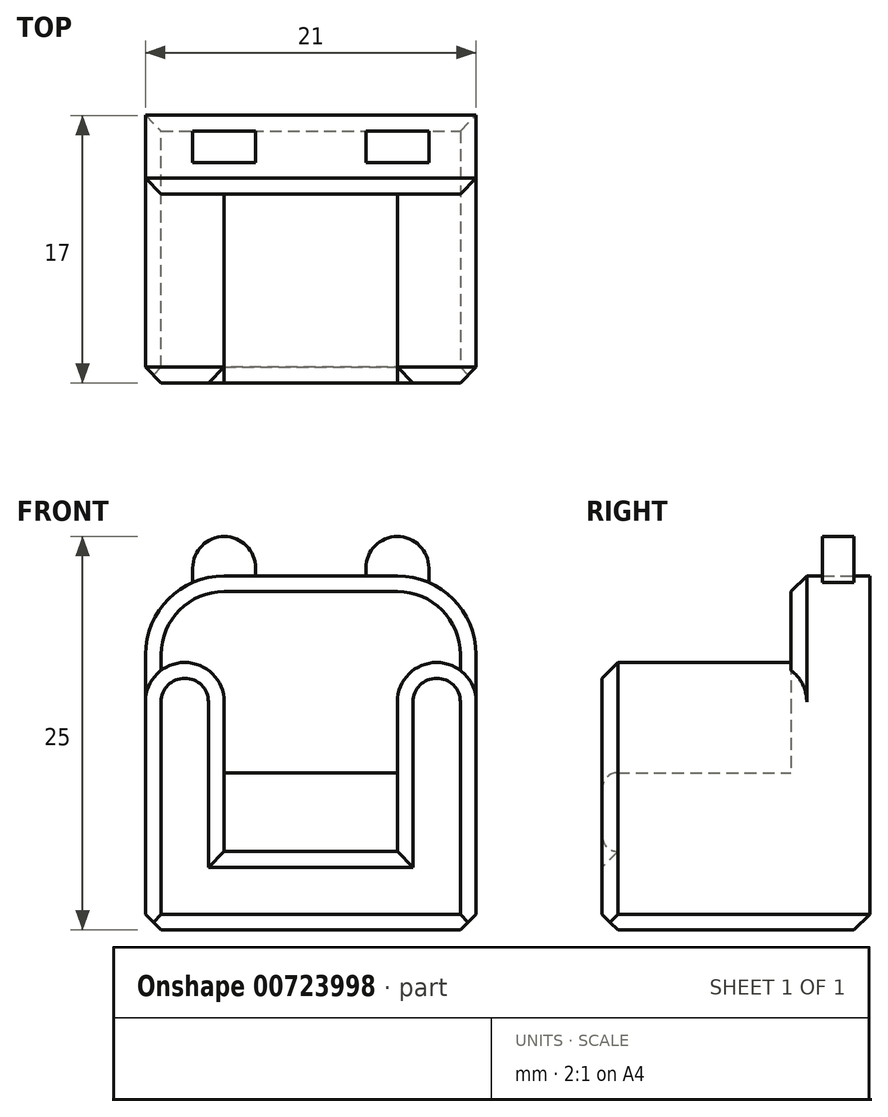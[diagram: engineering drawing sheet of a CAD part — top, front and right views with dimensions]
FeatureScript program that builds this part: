
annotation { "Feature Type Name" : "Feature", "Feature Type Description" : "" }
export const myFeature = defineFeature(function(context is Context, id is Id, definition is map)
    precondition{}
    {
        {
            var Q0;
            Q0=qCreatedBy(makeId("Top.planeOp"),FACE);
            var sketch = newSketch(context, id + "F0", { "sketchPlane" : qUnion([Q0])});
            skLineSegment(sketch, "E0.bottom", {"start": v(-12.68, 6.08) * mm, "end": v(8.32, 6.08) * mm});
            skLineSegment(sketch, "E0.top", {"start": v(-12.68, -10.92) * mm, "end": v(8.32, -10.92) * mm});
            skLineSegment(sketch, "E0.left", {"start": v(-12.68, 6.08) * mm, "end": v(-12.68, -10.92) * mm});
            skLineSegment(sketch, "E0.right", {"start": v(8.32, 6.08) * mm, "end": v(8.32, -10.92) * mm});
            skSolve(sketch);
        }
        {
            var Q0;
            Q0 = qSketchRegion(id + "F0", true);
            extrude(context, id + "F1", {"entities" : qUnion([Q0]), "depth" : 5 * mm, "offsetDistance" : 25 * mm});
        }
        {
            var Q0;
            Q0=makeQuery(id+"F1.opExtrude","CAP_FACE",FACE,{"disambiguationData":[OSD([sQuery(id+"F0.wireOp",EDGE,"E0.bottom"),sQuery(id+"F0.wireOp",EDGE,"E0.top"),sQuery(id+"F0.wireOp",EDGE,"E0.left"),sQuery(id+"F0.wireOp",EDGE,"E0.right")])],"isStart":false});
            var sketch = newSketch(context, id + "F2", { "sketchPlane" : qUnion([Q0])});
            skLineSegment(sketch, "E1.bottom", {"start": v(-12.68, 6.08) * mm, "end": v(8.32, 6.08) * mm});
            skLineSegment(sketch, "E1.top", {"start": v(-12.68, 1.08) * mm, "end": v(8.32, 1.08) * mm});
            skLineSegment(sketch, "E1.left", {"start": v(-12.68, 6.08) * mm, "end": v(-12.68, 1.08) * mm});
            skLineSegment(sketch, "E1.right", {"start": v(8.32, 6.08) * mm, "end": v(8.32, 1.08) * mm});
            skSolve(sketch);
        }
        {
            var Q0;
            Q0 = qSketchRegion(id + "F2", true);
            extrude(context, id + "F3", {"entities" : qUnion([Q0]), "operationType" : NewBodyOperationType.ADD, "depth" : 15 * mm, "offsetDistance" : 25 * mm});
        }
        {
            var Q0;
            Q0=makeQuery(id+"F1.opExtrude","SWEPT_FACE",FACE,{"disambiguationData":[OSD([sQuery(id+"F0.wireOp",EDGE,"E0.top")])]});
            var sketch = newSketch(context, id + "F4", { "sketchPlane" : qUnion([Q0])});
            skLineSegment(sketch, "E2.bottom", {"start": v(-12.68, 0) * mm, "end": v(-7.68, 0) * mm});
            skLineSegment(sketch, "E2.top", {"start": v(-12.68, 17) * mm, "end": v(-7.68, 17) * mm});
            skLineSegment(sketch, "E2.left", {"start": v(-12.68, 0) * mm, "end": v(-12.68, 17) * mm});
            skLineSegment(sketch, "E2.right", {"start": v(-7.68, 0) * mm, "end": v(-7.68, 17) * mm});
            skSolve(sketch);
        }
        {
            var Q0;
            Q0 = qSketchRegion(id + "F4", true);
            extrude(context, id + "F5", {"entities" : qUnion([Q0]), "operationType" : NewBodyOperationType.ADD, "oppositeDirection" : true, "depth" : 17 * mm, "offsetDistance" : 25 * mm});
        }
        {
            var Q0;
            Q0=makeQuery(id+"F5.boolean.opBoolean","MERGE",FACE,{"derivedFrom":[makeQuery(id+"F1.opExtrude","SWEPT_FACE",FACE,{"disambiguationData":[OSD([sQuery(id+"F0.wireOp",EDGE,"E0.top")])]}),makeQuery(id+"F5.opExtrude","CAP_FACE",FACE,{"disambiguationData":[OSD([sQuery(id+"F4.wireOp",EDGE,"E2.bottom"),sQuery(id+"F4.wireOp",EDGE,"E2.top"),sQuery(id+"F4.wireOp",EDGE,"E2.left"),sQuery(id+"F4.wireOp",EDGE,"E2.right")])],"isStart":true})]});
            var sketch = newSketch(context, id + "F6", { "sketchPlane" : qUnion([Q0])});
            skLineSegment(sketch, "E3.bottom", {"start": v(8.32, 0) * mm, "end": v(3.32, 0) * mm});
            skLineSegment(sketch, "E3.top", {"start": v(8.32, 17) * mm, "end": v(3.32, 17) * mm});
            skLineSegment(sketch, "E3.left", {"start": v(8.32, 0) * mm, "end": v(8.32, 17) * mm});
            skLineSegment(sketch, "E3.right", {"start": v(3.32, 0) * mm, "end": v(3.32, 17) * mm});
            skSolve(sketch);
        }
        {
            var Q0;
            Q0 = qSketchRegion(id + "F6", true);
            extrude(context, id + "F7", {"entities" : qUnion([Q0]), "operationType" : NewBodyOperationType.ADD, "oppositeDirection" : true, "depth" : 17 * mm, "offsetDistance" : 25 * mm});
        }
        {
            var Q0;
            Q0=makeQuery(id+"F5.opExtrude","SWEPT_EDGE",EDGE,{"disambiguationData":[OSD([sQuery(id+"F4.wireOp",EDGE,"E2.top"),sQuery(id+"F4.wireOp",EDGE,"E2.left")])]});
            fillet(context, id + "F8", {"entities" : qUnion([Q0]), "radius" : 2.5 * mm, "tangentPropagation" : true, "allowEdgeOverflow" : false});
        }
        {
            var Q0;
            Q0=makeQuery(id+"F5.opExtrude","SWEPT_EDGE",EDGE,{"disambiguationData":[OSD([sQuery(id+"F4.wireOp",EDGE,"E2.top"),sQuery(id+"F4.wireOp",EDGE,"E2.right")])]});
            fillet(context, id + "F9", {"entities" : qUnion([Q0]), "radius" : 2.5 * mm, "tangentPropagation" : true, "allowEdgeOverflow" : false});
        }
        {
            var Q0;
            Q0=makeQuery(id+"F7.opExtrude","SWEPT_EDGE",EDGE,{"disambiguationData":[OSD([sQuery(id+"F6.wireOp",EDGE,"E3.top"),sQuery(id+"F6.wireOp",EDGE,"E3.right")])]});
            fillet(context, id + "F10", {"entities" : qUnion([Q0]), "radius" : 2.5 * mm, "tangentPropagation" : true, "allowEdgeOverflow" : false});
        }
        {
            var Q0;
            Q0=makeQuery(id+"F7.opExtrude","SWEPT_EDGE",EDGE,{"disambiguationData":[OSD([sQuery(id+"F6.wireOp",EDGE,"E3.top"),sQuery(id+"F6.wireOp",EDGE,"E3.left")])]});
            fillet(context, id + "F11", {"entities" : qUnion([Q0]), "radius" : 2.5 * mm, "tangentPropagation" : true, "allowEdgeOverflow" : false});
        }
        {
            var Q0;
            Q0=makeQuery(id+"F1.opExtrude","CAP_EDGE",EDGE,{"disambiguationData":[OSD([sQuery(id+"F0.wireOp",EDGE,"E0.top")])],"isStart":false});
            var Q1;
            Q1=makeQuery(id+"F5.opExtrude","CAP_EDGE",EDGE,{"disambiguationData":[OSD([sQuery(id+"F4.wireOp",EDGE,"E2.right")])],"isStart":true});
            var Q2;
            Q2=makeQuery(id+"F7.boolean.opBoolean","MERGE",EDGE,{"derivedFrom":[makeQuery(id+"F1.opExtrude","SWEPT_EDGE",EDGE,{"disambiguationData":[OSD([sQuery(id+"F0.wireOp",EDGE,"E0.top"),sQuery(id+"F0.wireOp",EDGE,"E0.right")])]}),makeQuery(id+"F7.opExtrude","CAP_EDGE",EDGE,{"disambiguationData":[OSD([sQuery(id+"F6.wireOp",EDGE,"E3.left")])],"isStart":true})]});
            chamfer(context, id + "F12", {"entities" : qUnion([Q0, Q1, Q2]), "width" : 1 * mm, "tangentPropagation" : true});
        }
        {
            var Q0;
            Q0=makeQuery(id+"F1.opExtrude","CAP_EDGE",EDGE,{"disambiguationData":[OSD([sQuery(id+"F0.wireOp",EDGE,"E0.right")])],"isStart":true});
            var Q1;
            Q1=makeQuery(id+"F1.opExtrude","CAP_EDGE",EDGE,{"disambiguationData":[OSD([sQuery(id+"F0.wireOp",EDGE,"E0.top")])],"isStart":true});
            var Q2;
            Q2=makeQuery(id+"F1.opExtrude","CAP_EDGE",EDGE,{"disambiguationData":[OSD([sQuery(id+"F0.wireOp",EDGE,"E0.bottom")])],"isStart":true});
            var Q3;
            Q3=makeQuery(id+"F1.opExtrude","CAP_EDGE",EDGE,{"disambiguationData":[OSD([sQuery(id+"F0.wireOp",EDGE,"E0.left")])],"isStart":true});
            chamfer(context, id + "F13", {"entities" : qUnion([Q0, Q1, Q2, Q3]), "width" : 1 * mm, "tangentPropagation" : true});
        }
        {
            var Q0;
            Q0=makeQuery(id+"F1.opExtrude","CAP_FACE",FACE,{"disambiguationData":[OSD([sQuery(id+"F0.wireOp",EDGE,"E0.bottom"),sQuery(id+"F0.wireOp",EDGE,"E0.top"),sQuery(id+"F0.wireOp",EDGE,"E0.left"),sQuery(id+"F0.wireOp",EDGE,"E0.right")])],"isStart":false});
            var sketch = newSketch(context, id + "F14", { "sketchPlane" : qUnion([Q0])});
            skLineSegment(sketch, "E4.bottom", {"start": v(3.32, 1.08) * mm, "end": v(-7.68, 1.08) * mm});
            skLineSegment(sketch, "E4.top", {"start": v(3.32, -10.92) * mm, "end": v(-7.68, -10.92) * mm});
            skLineSegment(sketch, "E4.left", {"start": v(3.32, 1.08) * mm, "end": v(3.32, -10.92) * mm});
            skLineSegment(sketch, "E4.right", {"start": v(-7.68, 1.08) * mm, "end": v(-7.68, -10.92) * mm});
            skSolve(sketch);
        }
        {
            var Q0;
            Q0 = qSketchRegion(id + "F14", true);
            extrude(context, id + "F15", {"entities" : qUnion([Q0]), "operationType" : NewBodyOperationType.ADD, "depth" : 5 * mm, "offsetDistance" : 25 * mm});
        }
        {
            var Q0;
            Q0=makeQuery(id+"F15.opExtrude","CAP_EDGE",EDGE,{"disambiguationData":[OSD([sQuery(id+"F14.wireOp",EDGE,"E4.top")])],"isStart":false});
            fillet(context, id + "F16", {"entities" : qUnion([Q0]), "radius" : 1 * mm, "tangentPropagation" : true, "allowEdgeOverflow" : false});
        }
        {
            var Q0;
            Q0=makeQuery(id+"F15.opExtrude","CAP_EDGE",EDGE,{"disambiguationData":[OSD([sQuery(id+"F14.wireOp",EDGE,"E4.top")])],"isStart":true});
            fillet(context, id + "F17", {"entities" : qUnion([Q0]), "radius" : 1 * mm, "tangentPropagation" : true, "allowEdgeOverflow" : false});
        }
        {
            var Q0;
            Q0=makeQuery(id+"F3.opExtrude","CAP_FACE",FACE,{"disambiguationData":[OSD([sQuery(id+"F2.wireOp",EDGE,"E1.bottom"),sQuery(id+"F2.wireOp",EDGE,"E1.top"),sQuery(id+"F2.wireOp",EDGE,"E1.left"),sQuery(id+"F2.wireOp",EDGE,"E1.right")])],"isStart":false});
            extrude(context, id + "F18", {"entities" : qUnion([Q0]), "operationType" : NewBodyOperationType.ADD, "depth" : 2.5 * mm, "offsetDistance" : 25 * mm});
        }
        {
            var Q0;
            Q0=makeQuery(id+"F18.opExtrude","CAP_EDGE",EDGE,{"disambiguationData":[OSD([sQuery(id+"F2.wireOp",EDGE,"E1.left")])],"isStart":false});
            var Q1;
            Q1=makeQuery(id+"F18.opExtrude","CAP_EDGE",EDGE,{"disambiguationData":[OSD([sQuery(id+"F2.wireOp",EDGE,"E1.right")])],"isStart":false});
            fillet(context, id + "F19", {"entities" : qUnion([Q0, Q1]), "radius" : 5 * mm, "tangentPropagation" : true, "allowEdgeOverflow" : false});
        }
        {
            var Q0;
            {var subQ0=sQuery(id+"F2.wireOp",EDGE,"E1.top");Q0=makeQuery(id+"F19.opFillet","BLEND_EDGE",EDGE,{"blendedFrom":[makeQuery(id+"F18.opExtrude","CAP_EDGE",EDGE,{"disambiguationData":[OSD([sQuery(id+"F2.wireOp",EDGE,"E1.left")])],"isStart":false}),makeQuery(id+"F18.boolean.opBoolean","MERGE",FACE,{"derivedFrom":[makeQuery(id+"F3.opExtrude","SWEPT_FACE",FACE,{"disambiguationData":[OSD([subQ0])]}),makeQuery(id+"F18.opExtrude","SWEPT_FACE",FACE,{"disambiguationData":[OSD([subQ0])]})]})],"blendedInto":[makeQuery(id+"F18.boolean.opBoolean","MERGE",FACE,{"derivedFrom":[makeQuery(id+"F3.opExtrude","SWEPT_FACE",FACE,{"disambiguationData":[OSD([subQ0])]}),makeQuery(id+"F18.opExtrude","SWEPT_FACE",FACE,{"disambiguationData":[OSD([subQ0])]})]})]});}
            chamfer(context, id + "F20", {"entities" : qUnion([Q0]), "width" : 1 * mm, "tangentPropagation" : true});
        }
        {
            var Q0;
            Q0=qCreatedBy(makeId("Top.planeOp"),FACE);
            var sketch = newSketch(context, id + "F21", { "sketchPlane" : qUnion([Q0])});
            skLineSegment(sketch, "E5.bottom", {"start": v(-9.68, 5.08) * mm, "end": v(-5.68, 5.08) * mm});
            skLineSegment(sketch, "E5.top", {"start": v(-9.68, 3.08) * mm, "end": v(-5.68, 3.08) * mm});
            skLineSegment(sketch, "E5.left", {"start": v(-9.68, 5.08) * mm, "end": v(-9.68, 3.08) * mm});
            skLineSegment(sketch, "E5.right", {"start": v(-5.68, 5.08) * mm, "end": v(-5.68, 3.08) * mm});
            skLineSegment(sketch, "E6.bottom", {"start": v(1.32, 5.08) * mm, "end": v(5.32, 5.08) * mm});
            skLineSegment(sketch, "E6.top", {"start": v(1.32, 3.08) * mm, "end": v(5.32, 3.08) * mm});
            skLineSegment(sketch, "E6.left", {"start": v(1.32, 5.08) * mm, "end": v(1.32, 3.08) * mm});
            skLineSegment(sketch, "E6.right", {"start": v(5.32, 5.08) * mm, "end": v(5.32, 3.08) * mm});
            skSolve(sketch);
        }
        {
            var Q0;
            Q0=makeQuery(id+"F21.imprint","IMPRINT",FACE,{"disambiguationData":[TD([[makeQuery(id+"F21.imprint","IMPRINT",EDGE,{"derivedFrom":sQuery(id+"F21.wireOp",EDGE,"E5.bottom")}),-1.0]])]});
            extrude(context, id + "F22", {"entities" : qUnion([Q0]), "operationType" : NewBodyOperationType.ADD, "depth" : 25 * mm, "offsetDistance" : 25 * mm});
        }
        {
            var Q0;
            Q0=makeQuery(id+"F22.opExtrude","CAP_EDGE",EDGE,{"disambiguationData":[OSD([sQuery(id+"F21.wireOp",EDGE,"E5.left")])],"isStart":false});
            var Q1;
            Q1=makeQuery(id+"F22.opExtrude","CAP_EDGE",EDGE,{"disambiguationData":[OSD([sQuery(id+"F21.wireOp",EDGE,"E5.right")])],"isStart":false});
            fillet(context, id + "F23", {"entities" : qUnion([Q0, Q1]), "radius" : 2 * mm, "tangentPropagation" : true, "allowEdgeOverflow" : false});
        }
        {
            var Q0;
            Q0 = qSketchRegion(id + "F21", true);
            extrude(context, id + "F24", {"entities" : qUnion([Q0]), "operationType" : NewBodyOperationType.ADD, "depth" : 25 * mm, "offsetDistance" : 25 * mm});
        }
        {
            var Q0;
            Q0=makeQuery(id+"F24.opExtrude","CAP_EDGE",EDGE,{"disambiguationData":[OSD([sQuery(id+"F21.wireOp",EDGE,"E5.left")])],"isStart":false});
            var Q1;
            Q1=makeQuery(id+"F24.opExtrude","CAP_EDGE",EDGE,{"disambiguationData":[OSD([sQuery(id+"F21.wireOp",EDGE,"E5.right")])],"isStart":false});
            var Q2;
            Q2=makeQuery(id+"F24.opExtrude","CAP_EDGE",EDGE,{"disambiguationData":[OSD([sQuery(id+"F21.wireOp",EDGE,"E6.left")])],"isStart":false});
            var Q3;
            Q3=makeQuery(id+"F24.opExtrude","CAP_EDGE",EDGE,{"disambiguationData":[OSD([sQuery(id+"F21.wireOp",EDGE,"E6.right")])],"isStart":false});
            fillet(context, id + "F25", {"entities" : qUnion([Q0, Q1, Q2, Q3]), "radius" : 2 * mm, "tangentPropagation" : true, "allowEdgeOverflow" : false});
        }
    });
